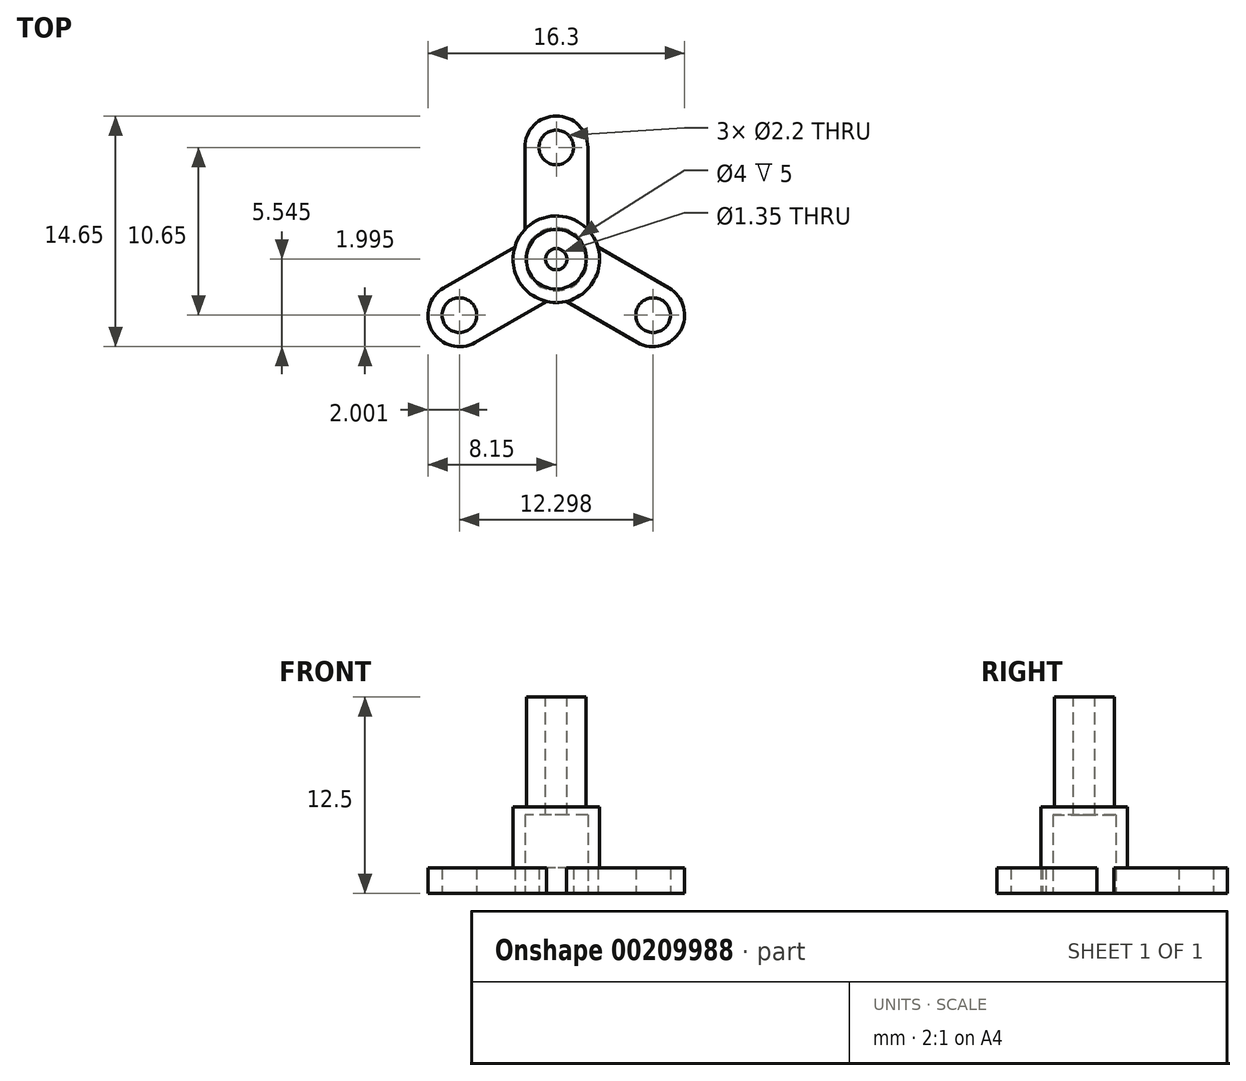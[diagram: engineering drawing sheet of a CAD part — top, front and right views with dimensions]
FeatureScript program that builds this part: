
annotation { "Feature Type Name" : "Feature", "Feature Type Description" : "" }
export const myFeature = defineFeature(function(context is Context, id is Id, definition is map)
    precondition{}
    {
        {
            var Q0;
            Q0=qCreatedBy(makeId("Top.planeOp"),FACE);
            var sketch = newSketch(context, id + "F0", { "sketchPlane" : qUnion([Q0])});
            skCircle(sketch, "E0", {"center": v(-11.04, 11.55) * mm, "radius": 2.75 * mm});
            skCircle(sketch, "E1", {"center": v(-11.04, 11.55) * mm, "radius": 2 * mm});
            skLineSegment(sketch, "E2", {"start": v(-11.04, 11.55) * mm, "end": v(-11.04, 23.86) * mm, "construction": true});
            skLineSegment(sketch, "E3", {"start": v(-11.04, 23.86) * mm, "end": v(-11.04, 11.55) * mm, "construction": true});
            skLineSegment(sketch, "E4", {"start": v(-11.04, 11.55) * mm, "end": v(3.9, 2.92) * mm, "construction": true});
            skLineSegment(sketch, "E5", {"start": v(-11.04, 11.55) * mm, "end": v(-25.98, 2.92) * mm, "construction": true});
            skCircle(sketch, "E6", {"center": v(-11.04, 13.55) * mm, "radius": 4 * mm, "construction": true});
            skLineSegment(sketch, "E7", {"start": v(-11.04, 17.55) * mm, "end": v(-6.47, 17.55) * mm, "construction": true});
            skLineSegment(sketch, "E8", {"start": v(-7.49, 17.55) * mm, "end": v(-7.49, 18.65) * mm, "construction": true});
            skLineSegment(sketch, "E9", {"start": v(-11.04, 11.55) * mm, "end": v(2.67, 19.46) * mm, "construction": true});
            skLineSegment(sketch, "E10", {"start": v(-9.04, 18.65) * mm, "end": v(-9.04, 13.43) * mm});
            skLineSegment(sketch, "E11.MirrorCS", {"start": v(-13.04, 18.65) * mm, "end": v(-13.04, 13.43) * mm});
            skLineSegment(sketch, "E12", {"start": v(-9.04, 13.43) * mm, "end": v(-9.04, 13.43) * mm});
            skLineSegment(sketch, "E13", {"start": v(-11.04, 14.3) * mm, "end": v(-6.28, 14.3) * mm, "construction": true});
            skLineSegment(sketch, "E14", {"start": v(-11.04, 13.55) * mm, "end": v(-0.7, 13.43) * mm, "construction": true});
            skLineSegment(sketch, "E15", {"start": v(-7.49, 18.65) * mm, "end": v(-16.51, 18.65) * mm, "construction": true});
            skCircle(sketch, "E16", {"center": v(-11.04, 18.65) * mm, "radius": 1.1 * mm});
            skPoint(sketch, "E17.orphan", {"position": v(-13.04, 18.35) * mm});
            skPoint(sketch, "E18.orphan", {"position": v(-9.04, 18.35) * mm});
            skArc(sketch, "E19", {"start": v(-9.04, 18.65) * mm, "mid": v(-11.04, 20.65) * mm, "end": v(-13.04, 18.65) * mm});
            skLineSegment(sketch, "E20.MirrorCS", {"start": v(-3.9, 9.73) * mm, "end": v(-8.4, 12.33) * mm});
            skCircle(sketch, "E21.MirrorC", {"center": v(-4.9, 8) * mm, "radius": 1.1 * mm});
            skArc(sketch, "E22.MirrorCS", {"start": v(-3.9, 9.73) * mm, "mid": v(-3.16, 7) * mm, "end": v(-5.9, 6.26) * mm});
            skLineSegment(sketch, "E23.MirrorCS", {"start": v(-5.9, 6.26) * mm, "end": v(-10.4, 8.87) * mm});
            skLineSegment(sketch, "E24.MirrorCS", {"start": v(-18.19, 9.73) * mm, "end": v(-13.67, 12.33) * mm});
            skCircle(sketch, "E25.MirrorC", {"center": v(-17.19, 8) * mm, "radius": 1.1 * mm});
            skLineSegment(sketch, "E26.MirrorCS", {"start": v(-16.19, 6.26) * mm, "end": v(-11.67, 8.87) * mm});
            skArc(sketch, "E27.MirrorCS", {"start": v(-18.19, 9.73) * mm, "mid": v(-18.92, 7) * mm, "end": v(-16.19, 6.26) * mm});
            skSolve(sketch);
        }
        {
            var Q0;
            {var subQ1=sQuery(id+"F0.wireOp",EDGE,"E10");Q0=makeQuery(id+"F0.imprint","IMPRINT",FACE,{"disambiguationData":[TD([[makeQuery(id+"F0.imprint","IMPRINT",EDGE,{"derivedFrom":subQ1}),-1.0]])]});}
            var Q1;
            {var subQ0=sQuery(id+"F0.wireOp",EDGE,"E24.MirrorCS");Q1=makeQuery(id+"F0.imprint","IMPRINT",FACE,{"disambiguationData":[TD([[makeQuery(id+"F0.imprint","IMPRINT",EDGE,{"derivedFrom":subQ0}),-1.0]])]});}
            var Q2;
            Q2=makeQuery(id+"F0.imprint","IMPRINT",FACE,{"disambiguationData":[TD([[makeQuery(id+"F0.imprint","IMPRINT",EDGE,{"derivedFrom":sQuery(id+"F0.wireOp",EDGE,"E1")}),-1.0]])]});
            var Q3;
            {var subQ0=sQuery(id+"F0.wireOp",EDGE,"E20.MirrorCS");Q3=makeQuery(id+"F0.imprint","IMPRINT",FACE,{"disambiguationData":[TD([[makeQuery(id+"F0.imprint","IMPRINT",EDGE,{"derivedFrom":subQ0}),1.0]])]});}
            extrude(context, id + "F1", {"entities" : qUnion([Q0, Q1, Q2, Q3]), "depth" : 1.65 * mm});
        }
        {
            var Q0;
            Q0=makeQuery(id+"F1.opExtrude","CAP_FACE",FACE,{"disambiguationData":[OSD([sQuery(id+"F0.wireOp",EDGE,"E0"),sQuery(id+"F0.wireOp",EDGE,"E1"),sQuery(id+"F0.wireOp",EDGE,"E10"),sQuery(id+"F0.wireOp",EDGE,"E11.MirrorCS"),sQuery(id+"F0.wireOp",EDGE,"E16"),sQuery(id+"F0.wireOp",EDGE,"E19"),sQuery(id+"F0.wireOp",EDGE,"E20.MirrorCS"),sQuery(id+"F0.wireOp",EDGE,"E21.MirrorC"),sQuery(id+"F0.wireOp",EDGE,"E22.MirrorCS"),sQuery(id+"F0.wireOp",EDGE,"E23.MirrorCS"),sQuery(id+"F0.wireOp",EDGE,"E24.MirrorCS"),sQuery(id+"F0.wireOp",EDGE,"E25.MirrorC"),sQuery(id+"F0.wireOp",EDGE,"E26.MirrorCS"),sQuery(id+"F0.wireOp",EDGE,"E27.MirrorCS")])],"isStart":false});
            var sketch = newSketch(context, id + "F2", { "sketchPlane" : qUnion([Q0])});
            skPoint(sketch, "E28.first.point", {"position": v(-9.04, 13.43) * mm});
            skPoint(sketch, "E28.second.point", {"position": v(-9.04, 13.43) * mm});
            skPoint(sketch, "E28.third.point", {"position": v(-9.04, 13.43) * mm});
            skCircle(sketch, "E29", {"center": v(-11.04, 11.55) * mm, "radius": 2.75 * mm});
            skPoint(sketch, "E29.first.point", {"position": v(-13.67, 12.33) * mm});
            skPoint(sketch, "E29.third.point", {"position": v(-11.67, 8.87) * mm});
            skCircle(sketch, "E30", {"center": v(-11.04, 11.55) * mm, "radius": 2 * mm});
            skPoint(sketch, "E30.first.point", {"position": v(-11.02, 13.55) * mm});
            skPoint(sketch, "E30.second.point", {"position": v(-12.74, 10.5) * mm});
            skPoint(sketch, "E30.third.point", {"position": v(-9.3, 10.56) * mm});
            skSolve(sketch);
        }
        {
            var Q0;
            Q0=makeQuery(id+"F2.imprint","IMPRINT",FACE,{"disambiguationData":[TD([[makeQuery(id+"F2.imprint","IMPRINT",EDGE,{"derivedFrom":sQuery(id+"F2.wireOp",EDGE,"E30")}),-1.0]])]});
            extrude(context, id + "F3", {"entities" : qUnion([Q0]), "operationType" : NewBodyOperationType.ADD, "depth" : 3.85 * mm});
        }
        {
            var Q0;
            Q0=makeQuery(id+"F3.opExtrude","CAP_FACE",FACE,{"disambiguationData":[OSD([sQuery(id+"F2.wireOp",EDGE,"E29"),sQuery(id+"F2.wireOp",EDGE,"E30")])],"isStart":false});
            var sketch = newSketch(context, id + "F4", { "sketchPlane" : qUnion([Q0])});
            skCircle(sketch, "E31", {"center": v(-11.04, 11.55) * mm, "radius": 2 * mm});
            skPoint(sketch, "E31.first.point", {"position": v(-11.97, 13.31) * mm});
            skPoint(sketch, "E31.second.point", {"position": v(-12.47, 10.14) * mm});
            skPoint(sketch, "E31.third.point", {"position": v(-9.15, 10.88) * mm});
            skCircle(sketch, "E32", {"center": v(-11.04, 11.55) * mm, "radius": 1.9 * mm});
            skCircle(sketch, "E33", {"center": v(-11.04, 11.55) * mm, "radius": 0.68 * mm});
            skSolve(sketch);
        }
        {
            var Q0;
            Q0=makeQuery(id+"F4.imprint","IMPRINT",FACE,{"disambiguationData":[TD([[makeQuery(id+"F4.imprint","IMPRINT",EDGE,{"derivedFrom":sQuery(id+"F4.wireOp",EDGE,"E31")}),1.0]])]});
            var Q1;
            Q1=makeQuery(id+"F4.imprint","IMPRINT",FACE,{"disambiguationData":[TD([[makeQuery(id+"F4.imprint","IMPRINT",EDGE,{"derivedFrom":sQuery(id+"F4.wireOp",EDGE,"E32")}),1.0]])]});
            extrude(context, id + "F5", {"entities" : qUnion([Q0, Q1]), "operationType" : NewBodyOperationType.ADD, "oppositeDirection" : true, "depth" : 0.5 * mm});
        }
        {
            var Q0;
            Q0=makeQuery(id+"F4.imprint","IMPRINT",FACE,{"disambiguationData":[TD([[makeQuery(id+"F4.imprint","IMPRINT",EDGE,{"derivedFrom":sQuery(id+"F4.wireOp",EDGE,"E32")}),1.0]])]});
            extrude(context, id + "F6", {"entities" : qUnion([Q0]), "operationType" : NewBodyOperationType.ADD, "depth" : 7 * mm});
        }
    });
